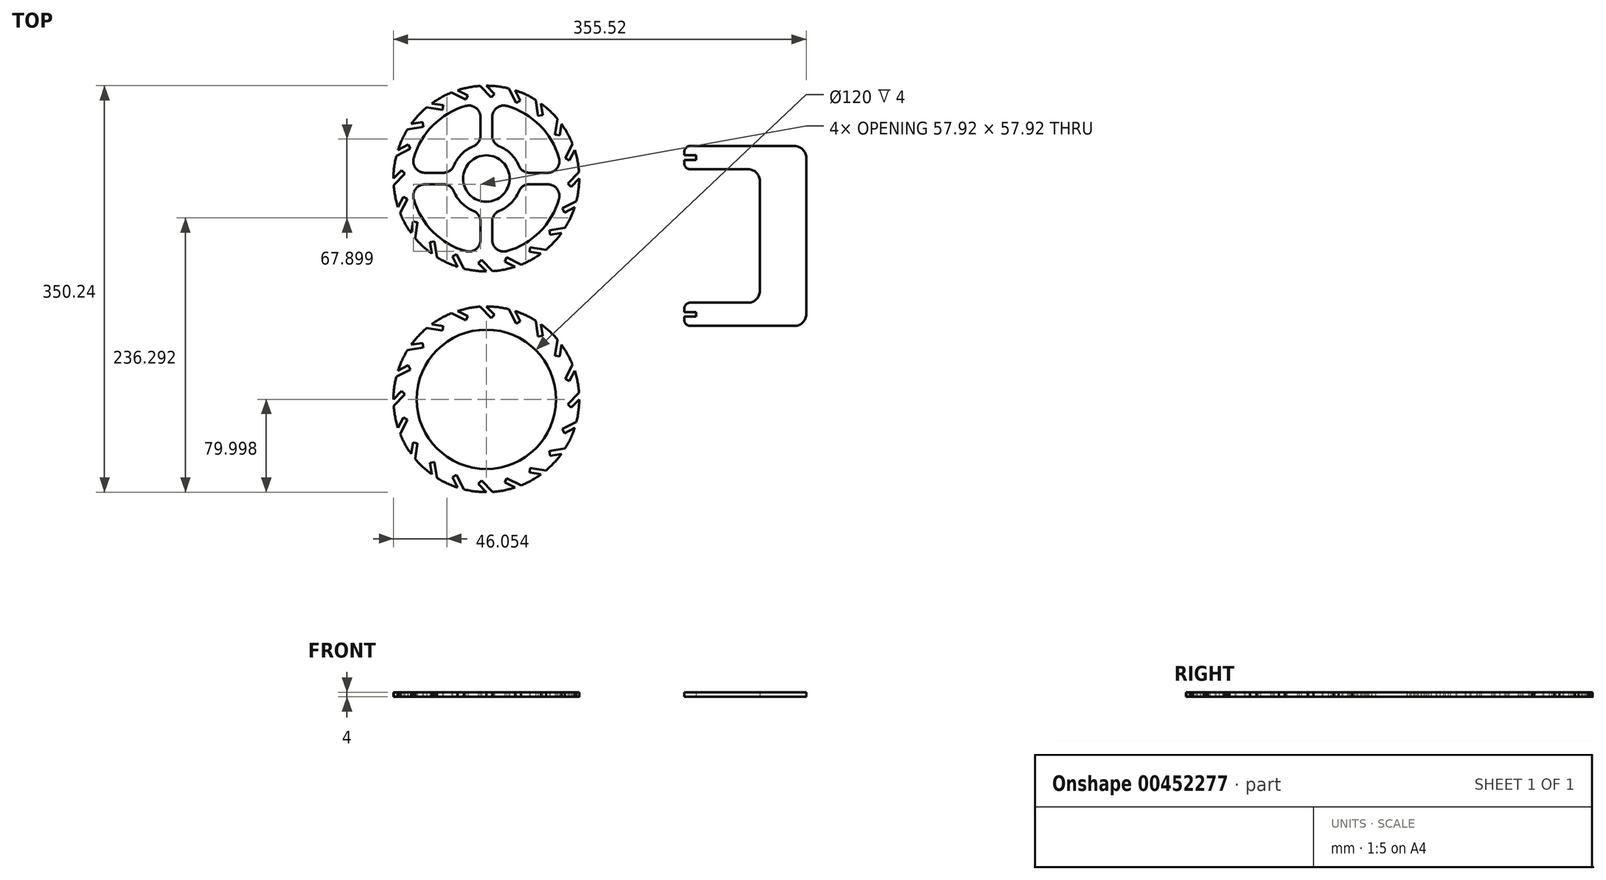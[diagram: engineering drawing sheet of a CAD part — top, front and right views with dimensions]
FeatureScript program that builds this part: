
annotation { "Feature Type Name" : "Feature", "Feature Type Description" : "" }
export const myFeature = defineFeature(function(context is Context, id is Id, definition is map)
    precondition{}
    {
        {
            var Q0;
            Q0=qCreatedBy(makeId("Top.planeOp"),FACE);
            var sketch = newSketch(context, id + "F0", { "sketchPlane" : qUnion([Q0])});
            skLineSegment(sketch, "E0", {"start": v(-117.76, 175.12) * mm, "end": v(-110.69, 168.05) * mm});
            skLineSegment(sketch, "E1", {"start": v(-110.69, 168.05) * mm, "end": v(-113.51, 165.22) * mm});
            skLineSegment(sketch, "E2", {"start": v(-133.57, 166.67) * mm, "end": v(-135.38, 163.1) * mm});
            skLineSegment(sketch, "E3", {"start": v(-142.48, 171.2) * mm, "end": v(-133.57, 166.67) * mm});
            skLineSegment(sketch, "E4", {"start": v(-135.38, 163.1) * mm, "end": v(-147.62, 169.34) * mm});
            skLineSegment(sketch, "E5", {"start": v(-154.9, 158.28) * mm, "end": v(-155.53, 154.33) * mm});
            skLineSegment(sketch, "E6", {"start": v(-164.78, 159.84) * mm, "end": v(-154.9, 158.28) * mm});
            skLineSegment(sketch, "E7", {"start": v(-155.53, 154.33) * mm, "end": v(-169.1, 156.48) * mm});
            skLineSegment(sketch, "E8", {"start": v(-172.6, 143.7) * mm, "end": v(-171.98, 139.76) * mm});
            skLineSegment(sketch, "E9", {"start": v(-182.48, 142.14) * mm, "end": v(-172.6, 143.7) * mm});
            skLineSegment(sketch, "E10", {"start": v(-171.98, 139.76) * mm, "end": v(-185.54, 137.6) * mm});
            skLineSegment(sketch, "E11", {"start": v(-184.93, 124.38) * mm, "end": v(-183.11, 120.82) * mm});
            skLineSegment(sketch, "E12", {"start": v(-193.84, 119.84) * mm, "end": v(-184.93, 124.38) * mm});
            skLineSegment(sketch, "E13", {"start": v(-183.11, 120.82) * mm, "end": v(-195.35, 114.58) * mm});
            skLineSegment(sketch, "E14", {"start": v(-190.69, 102.2) * mm, "end": v(-187.86, 99.36) * mm});
            skLineSegment(sketch, "E15", {"start": v(-197.76, 95.12) * mm, "end": v(-190.69, 102.2) * mm});
            skLineSegment(sketch, "E16", {"start": v(-187.86, 99.36) * mm, "end": v(-197.57, 89.65) * mm});
            skLineSegment(sketch, "E17", {"start": v(-189.3, 79.31) * mm, "end": v(-185.74, 77.5) * mm});
            skLineSegment(sketch, "E18", {"start": v(-193.84, 70.4) * mm, "end": v(-189.3, 79.31) * mm});
            skLineSegment(sketch, "E19", {"start": v(-185.74, 77.5) * mm, "end": v(-191.97, 65.26) * mm});
            skLineSegment(sketch, "E20", {"start": v(-180.91, 57.98) * mm, "end": v(-176.96, 57.35) * mm});
            skLineSegment(sketch, "E21", {"start": v(-182.48, 48.1) * mm, "end": v(-180.91, 57.98) * mm});
            skLineSegment(sketch, "E22", {"start": v(-176.96, 57.35) * mm, "end": v(-179.11, 43.78) * mm});
            skLineSegment(sketch, "E23", {"start": v(-166.34, 40.28) * mm, "end": v(-162.4, 40.9) * mm});
            skLineSegment(sketch, "E24", {"start": v(-164.78, 30.4) * mm, "end": v(-166.34, 40.28) * mm});
            skLineSegment(sketch, "E25", {"start": v(-162.4, 40.9) * mm, "end": v(-160.24, 27.34) * mm});
            skLineSegment(sketch, "E26", {"start": v(-147.02, 27.95) * mm, "end": v(-143.45, 29.76) * mm});
            skLineSegment(sketch, "E27", {"start": v(-142.48, 19.04) * mm, "end": v(-147.02, 27.95) * mm});
            skLineSegment(sketch, "E28", {"start": v(-143.45, 29.76) * mm, "end": v(-137.22, 17.52) * mm});
            skLineSegment(sketch, "E29", {"start": v(-124.83, 22.2) * mm, "end": v(-122, 25.02) * mm});
            skLineSegment(sketch, "E30", {"start": v(-117.76, 15.12) * mm, "end": v(-124.83, 22.2) * mm});
            skLineSegment(sketch, "E31", {"start": v(-122, 25.02) * mm, "end": v(-112.29, 15.3) * mm});
            skLineSegment(sketch, "E32", {"start": v(-101.95, 23.58) * mm, "end": v(-100.13, 27.14) * mm});
            skLineSegment(sketch, "E33", {"start": v(-93.04, 19.04) * mm, "end": v(-101.95, 23.58) * mm});
            skLineSegment(sketch, "E34", {"start": v(-100.13, 27.14) * mm, "end": v(-87.9, 20.9) * mm});
            skLineSegment(sketch, "E35", {"start": v(-80.61, 31.96) * mm, "end": v(-79.98, 35.92) * mm});
            skLineSegment(sketch, "E36", {"start": v(-70.73, 30.4) * mm, "end": v(-80.61, 31.96) * mm});
            skLineSegment(sketch, "E37", {"start": v(-79.98, 35.92) * mm, "end": v(-66.42, 33.77) * mm});
            skLineSegment(sketch, "E38", {"start": v(-62.91, 46.53) * mm, "end": v(-63.54, 50.49) * mm});
            skLineSegment(sketch, "E39", {"start": v(-53.04, 48.1) * mm, "end": v(-62.91, 46.53) * mm});
            skLineSegment(sketch, "E40", {"start": v(-63.54, 50.49) * mm, "end": v(-49.97, 52.63) * mm});
            skLineSegment(sketch, "E41", {"start": v(-50.58, 65.86) * mm, "end": v(-52.4, 69.42) * mm});
            skLineSegment(sketch, "E42", {"start": v(-41.67, 70.4) * mm, "end": v(-50.58, 65.86) * mm});
            skLineSegment(sketch, "E43", {"start": v(-52.4, 69.42) * mm, "end": v(-40.16, 75.66) * mm});
            skLineSegment(sketch, "E44", {"start": v(-44.83, 88.05) * mm, "end": v(-47.66, 90.88) * mm});
            skLineSegment(sketch, "E45", {"start": v(-37.76, 95.12) * mm, "end": v(-44.83, 88.05) * mm});
            skLineSegment(sketch, "E46", {"start": v(-47.66, 90.88) * mm, "end": v(-37.94, 100.6) * mm});
            skLineSegment(sketch, "E47", {"start": v(-46.21, 110.93) * mm, "end": v(-49.78, 112.75) * mm});
            skLineSegment(sketch, "E48", {"start": v(-41.67, 119.84) * mm, "end": v(-46.21, 110.93) * mm});
            skLineSegment(sketch, "E49", {"start": v(-49.78, 112.75) * mm, "end": v(-43.54, 124.99) * mm});
            skLineSegment(sketch, "E50", {"start": v(-54.6, 132.27) * mm, "end": v(-58.55, 132.9) * mm});
            skLineSegment(sketch, "E51", {"start": v(-53.04, 142.14) * mm, "end": v(-54.6, 132.27) * mm});
            skLineSegment(sketch, "E52", {"start": v(-58.55, 132.9) * mm, "end": v(-56.4, 146.46) * mm});
            skLineSegment(sketch, "E53", {"start": v(-69.17, 149.97) * mm, "end": v(-73.12, 149.34) * mm});
            skLineSegment(sketch, "E54", {"start": v(-70.73, 159.84) * mm, "end": v(-69.17, 149.97) * mm});
            skLineSegment(sketch, "E55", {"start": v(-73.12, 149.34) * mm, "end": v(-75.27, 162.9) * mm});
            skLineSegment(sketch, "E56", {"start": v(-88.5, 162.3) * mm, "end": v(-92.06, 160.48) * mm});
            skLineSegment(sketch, "E57", {"start": v(-93.04, 171.2) * mm, "end": v(-88.5, 162.3) * mm});
            skLineSegment(sketch, "E58", {"start": v(-92.06, 160.48) * mm, "end": v(-98.3, 172.72) * mm});
            skArc(sketch, "E59", {"start": v(-123.23, 174.93) * mm, "mid": v(-132.97, 173.66) * mm, "end": v(-142.48, 171.2) * mm});
            skArc(sketch, "E60", {"start": v(-169.1, 156.48) * mm, "mid": v(-176.23, 149.72) * mm, "end": v(-182.48, 142.14) * mm});
            skArc(sketch, "E61", {"start": v(-185.54, 137.6) * mm, "mid": v(-190.24, 128.98) * mm, "end": v(-193.84, 119.84) * mm});
            skArc(sketch, "E62", {"start": v(-195.35, 114.58) * mm, "mid": v(-197.15, 104.93) * mm, "end": v(-197.76, 95.12) * mm});
            skArc(sketch, "E63", {"start": v(-197.57, 89.65) * mm, "mid": v(-196.3, 79.91) * mm, "end": v(-193.84, 70.4) * mm});
            skArc(sketch, "E64", {"start": v(-191.97, 65.26) * mm, "mid": v(-187.75, 56.39) * mm, "end": v(-182.48, 48.1) * mm});
            skArc(sketch, "E65", {"start": v(-179.11, 43.78) * mm, "mid": v(-172.36, 36.65) * mm, "end": v(-164.78, 30.4) * mm});
            skArc(sketch, "E66", {"start": v(-160.24, 27.34) * mm, "mid": v(-151.62, 22.64) * mm, "end": v(-142.48, 19.04) * mm});
            skArc(sketch, "E67", {"start": v(-137.22, 17.52) * mm, "mid": v(-127.56, 15.72) * mm, "end": v(-117.76, 15.12) * mm});
            skArc(sketch, "E68", {"start": v(-112.29, 15.3) * mm, "mid": v(-102.55, 16.58) * mm, "end": v(-93.04, 19.04) * mm});
            skArc(sketch, "E69", {"start": v(-87.9, 20.9) * mm, "mid": v(-79.02, 25.13) * mm, "end": v(-70.73, 30.4) * mm});
            skArc(sketch, "E70", {"start": v(-66.42, 33.77) * mm, "mid": v(-59.29, 40.52) * mm, "end": v(-53.04, 48.1) * mm});
            skArc(sketch, "E71", {"start": v(-49.97, 52.63) * mm, "mid": v(-45.28, 61.26) * mm, "end": v(-41.67, 70.4) * mm});
            skArc(sketch, "E72", {"start": v(-40.16, 75.66) * mm, "mid": v(-38.36, 85.32) * mm, "end": v(-37.76, 95.12) * mm});
            skArc(sketch, "E73", {"start": v(-37.94, 100.6) * mm, "mid": v(-39.22, 110.33) * mm, "end": v(-41.67, 119.84) * mm});
            skArc(sketch, "E74", {"start": v(-43.54, 124.99) * mm, "mid": v(-47.76, 133.86) * mm, "end": v(-53.04, 142.14) * mm});
            skArc(sketch, "E75", {"start": v(-56.4, 146.46) * mm, "mid": v(-63.16, 153.6) * mm, "end": v(-70.73, 159.84) * mm});
            skArc(sketch, "E76", {"start": v(-98.3, 172.72) * mm, "mid": v(-107.95, 174.52) * mm, "end": v(-117.76, 175.12) * mm});
            skArc(sketch, "E77", {"start": v(-75.27, 162.9) * mm, "mid": v(-83.9, 167.6) * mm, "end": v(-93.04, 171.2) * mm});
            skLineSegment(sketch, "E78", {"start": v(-154.84, 90.13) * mm, "end": v(-170.67, 90.13) * mm});
            skLineSegment(sketch, "E79", {"start": v(-154.84, 100.11) * mm, "end": v(-170.67, 100.11) * mm});
            skLineSegment(sketch, "E80", {"start": v(-122.75, 58.04) * mm, "end": v(-122.75, 42.2) * mm});
            skLineSegment(sketch, "E81", {"start": v(-112.76, 58.04) * mm, "end": v(-112.76, 42.2) * mm});
            skLineSegment(sketch, "E82", {"start": v(-80.67, 90.13) * mm, "end": v(-64.84, 90.13) * mm});
            skLineSegment(sketch, "E83", {"start": v(-80.67, 100.11) * mm, "end": v(-64.84, 100.11) * mm});
            skLineSegment(sketch, "E84", {"start": v(-112.76, 132.2) * mm, "end": v(-112.76, 148.04) * mm});
            skLineSegment(sketch, "E85", {"start": v(-122.75, 132.2) * mm, "end": v(-122.75, 148.04) * mm});
            skArc(sketch, "E86", {"start": v(-145.57, 83.88) * mm, "mid": v(-138.97, 73.9) * mm, "end": v(-129, 67.3) * mm});
            skArc(sketch, "E87", {"start": v(-180.3, 77.4) * mm, "mid": v(-163.72, 49.16) * mm, "end": v(-135.47, 32.58) * mm});
            skArc(sketch, "E88", {"start": v(-106.51, 67.3) * mm, "mid": v(-96.54, 73.9) * mm, "end": v(-89.94, 83.88) * mm});
            skArc(sketch, "E89", {"start": v(-100.04, 32.58) * mm, "mid": v(-71.8, 49.16) * mm, "end": v(-55.22, 77.4) * mm});
            skArc(sketch, "E90", {"start": v(-135.47, 157.66) * mm, "mid": v(-163.72, 141.08) * mm, "end": v(-180.3, 112.84) * mm});
            skArc(sketch, "E91", {"start": v(-55.22, 112.84) * mm, "mid": v(-71.8, 141.08) * mm, "end": v(-100.04, 157.66) * mm});
            skArc(sketch, "E92", {"start": v(-129, 122.93) * mm, "mid": v(-138.97, 116.33) * mm, "end": v(-145.57, 106.37) * mm});
            skArc(sketch, "E93", {"start": v(-89.94, 106.37) * mm, "mid": v(-96.54, 116.33) * mm, "end": v(-106.51, 122.93) * mm});
            skArc(sketch, "E94", {"start": v(-180.3, 112.84) * mm, "mid": v(-178.65, 104.08) * mm, "end": v(-170.67, 100.11) * mm});
            skArc(sketch, "E95", {"start": v(-154.84, 100.11) * mm, "mid": v(-149.25, 101.82) * mm, "end": v(-145.57, 106.37) * mm});
            skArc(sketch, "E96", {"start": v(-129, 122.93) * mm, "mid": v(-124.46, 126.61) * mm, "end": v(-122.75, 132.2) * mm});
            skArc(sketch, "E97", {"start": v(-112.76, 132.2) * mm, "mid": v(-111.06, 126.61) * mm, "end": v(-106.51, 122.93) * mm});
            skArc(sketch, "E98", {"start": v(-89.94, 106.37) * mm, "mid": v(-86.26, 101.82) * mm, "end": v(-80.67, 100.11) * mm});
            skArc(sketch, "E99", {"start": v(-80.67, 90.13) * mm, "mid": v(-86.26, 88.42) * mm, "end": v(-89.94, 83.88) * mm});
            skArc(sketch, "E100", {"start": v(-106.51, 67.3) * mm, "mid": v(-111.06, 63.63) * mm, "end": v(-112.76, 58.04) * mm});
            skArc(sketch, "E101", {"start": v(-122.75, 58.04) * mm, "mid": v(-124.46, 63.63) * mm, "end": v(-129, 67.3) * mm});
            skArc(sketch, "E102", {"start": v(-145.57, 83.88) * mm, "mid": v(-149.25, 88.42) * mm, "end": v(-154.84, 90.13) * mm});
            skArc(sketch, "E103", {"start": v(-122.75, 148.04) * mm, "mid": v(-126.72, 156.02) * mm, "end": v(-135.47, 157.66) * mm});
            skArc(sketch, "E104", {"start": v(-100.04, 157.66) * mm, "mid": v(-108.8, 156.02) * mm, "end": v(-112.76, 148.04) * mm});
            skArc(sketch, "E105", {"start": v(-64.84, 100.11) * mm, "mid": v(-56.86, 104.08) * mm, "end": v(-55.22, 112.84) * mm});
            skArc(sketch, "E106", {"start": v(-55.22, 77.4) * mm, "mid": v(-56.86, 86.16) * mm, "end": v(-64.84, 90.13) * mm});
            skArc(sketch, "E107", {"start": v(-112.76, 42.2) * mm, "mid": v(-108.8, 34.23) * mm, "end": v(-100.04, 32.58) * mm});
            skArc(sketch, "E108", {"start": v(-135.47, 32.58) * mm, "mid": v(-126.72, 34.23) * mm, "end": v(-122.75, 42.2) * mm});
            skArc(sketch, "E109", {"start": v(-170.67, 90.13) * mm, "mid": v(-178.65, 86.16) * mm, "end": v(-180.3, 77.4) * mm});
            skCircle(sketch, "E110", {"center": v(-117.76, 95.12) * mm, "radius": 20 * mm});
            skLineSegment(sketch, "E111", {"start": v(-113.51, 165.22) * mm, "end": v(-123.23, 174.93) * mm});
            skLineSegment(sketch, "E112", {"start": v(-117.76, -15.12) * mm, "end": v(-110.69, -22.2) * mm});
            skLineSegment(sketch, "E113", {"start": v(-110.69, -22.2) * mm, "end": v(-113.51, -25.02) * mm});
            skLineSegment(sketch, "E114", {"start": v(-133.57, -23.58) * mm, "end": v(-135.38, -27.14) * mm});
            skLineSegment(sketch, "E115", {"start": v(-142.48, -19.04) * mm, "end": v(-133.57, -23.58) * mm});
            skLineSegment(sketch, "E116", {"start": v(-135.38, -27.14) * mm, "end": v(-147.62, -20.9) * mm});
            skLineSegment(sketch, "E117", {"start": v(-154.9, -31.96) * mm, "end": v(-155.53, -35.92) * mm});
            skLineSegment(sketch, "E118", {"start": v(-164.78, -30.4) * mm, "end": v(-154.9, -31.96) * mm});
            skLineSegment(sketch, "E119", {"start": v(-155.53, -35.92) * mm, "end": v(-169.1, -33.77) * mm});
            skLineSegment(sketch, "E120", {"start": v(-172.6, -46.53) * mm, "end": v(-171.98, -50.49) * mm});
            skLineSegment(sketch, "E121", {"start": v(-182.48, -48.1) * mm, "end": v(-172.6, -46.53) * mm});
            skLineSegment(sketch, "E122", {"start": v(-171.98, -50.49) * mm, "end": v(-185.54, -52.63) * mm});
            skLineSegment(sketch, "E123", {"start": v(-184.93, -65.86) * mm, "end": v(-183.11, -69.42) * mm});
            skLineSegment(sketch, "E124", {"start": v(-193.84, -70.4) * mm, "end": v(-184.93, -65.86) * mm});
            skLineSegment(sketch, "E125", {"start": v(-183.11, -69.42) * mm, "end": v(-195.35, -75.66) * mm});
            skLineSegment(sketch, "E126", {"start": v(-190.69, -88.05) * mm, "end": v(-187.86, -90.88) * mm});
            skLineSegment(sketch, "E127", {"start": v(-197.76, -95.12) * mm, "end": v(-190.69, -88.05) * mm});
            skLineSegment(sketch, "E128", {"start": v(-187.86, -90.88) * mm, "end": v(-197.57, -100.6) * mm});
            skLineSegment(sketch, "E129", {"start": v(-189.3, -110.93) * mm, "end": v(-185.74, -112.75) * mm});
            skLineSegment(sketch, "E130", {"start": v(-193.84, -119.84) * mm, "end": v(-189.3, -110.93) * mm});
            skLineSegment(sketch, "E131", {"start": v(-185.74, -112.75) * mm, "end": v(-191.97, -124.99) * mm});
            skLineSegment(sketch, "E132", {"start": v(-180.91, -132.27) * mm, "end": v(-176.96, -132.9) * mm});
            skLineSegment(sketch, "E133", {"start": v(-182.48, -142.14) * mm, "end": v(-180.91, -132.27) * mm});
            skLineSegment(sketch, "E134", {"start": v(-176.96, -132.9) * mm, "end": v(-179.11, -146.46) * mm});
            skLineSegment(sketch, "E135", {"start": v(-166.34, -149.97) * mm, "end": v(-162.4, -149.34) * mm});
            skLineSegment(sketch, "E136", {"start": v(-164.78, -159.84) * mm, "end": v(-166.34, -149.97) * mm});
            skLineSegment(sketch, "E137", {"start": v(-162.4, -149.34) * mm, "end": v(-160.24, -162.9) * mm});
            skLineSegment(sketch, "E138", {"start": v(-147.02, -162.3) * mm, "end": v(-143.45, -160.48) * mm});
            skLineSegment(sketch, "E139", {"start": v(-142.48, -171.2) * mm, "end": v(-147.02, -162.3) * mm});
            skLineSegment(sketch, "E140", {"start": v(-143.45, -160.48) * mm, "end": v(-137.22, -172.72) * mm});
            skLineSegment(sketch, "E141", {"start": v(-124.83, -168.05) * mm, "end": v(-122, -165.22) * mm});
            skLineSegment(sketch, "E142", {"start": v(-117.76, -175.12) * mm, "end": v(-124.83, -168.05) * mm});
            skLineSegment(sketch, "E143", {"start": v(-122, -165.22) * mm, "end": v(-112.29, -174.93) * mm});
            skLineSegment(sketch, "E144", {"start": v(-101.95, -166.67) * mm, "end": v(-100.13, -163.1) * mm});
            skLineSegment(sketch, "E145", {"start": v(-93.04, -171.2) * mm, "end": v(-101.95, -166.67) * mm});
            skLineSegment(sketch, "E146", {"start": v(-100.13, -163.1) * mm, "end": v(-87.9, -169.34) * mm});
            skLineSegment(sketch, "E147", {"start": v(-80.61, -158.28) * mm, "end": v(-79.98, -154.33) * mm});
            skLineSegment(sketch, "E148", {"start": v(-70.73, -159.84) * mm, "end": v(-80.61, -158.28) * mm});
            skLineSegment(sketch, "E149", {"start": v(-79.98, -154.33) * mm, "end": v(-66.42, -156.48) * mm});
            skLineSegment(sketch, "E150", {"start": v(-62.91, -143.7) * mm, "end": v(-63.54, -139.76) * mm});
            skLineSegment(sketch, "E151", {"start": v(-53.04, -142.14) * mm, "end": v(-62.91, -143.7) * mm});
            skLineSegment(sketch, "E152", {"start": v(-63.54, -139.76) * mm, "end": v(-49.97, -137.6) * mm});
            skLineSegment(sketch, "E153", {"start": v(-50.58, -124.38) * mm, "end": v(-52.4, -120.82) * mm});
            skLineSegment(sketch, "E154", {"start": v(-41.67, -119.84) * mm, "end": v(-50.58, -124.38) * mm});
            skLineSegment(sketch, "E155", {"start": v(-52.4, -120.82) * mm, "end": v(-40.16, -114.58) * mm});
            skLineSegment(sketch, "E156", {"start": v(-44.83, -102.2) * mm, "end": v(-47.66, -99.36) * mm});
            skLineSegment(sketch, "E157", {"start": v(-37.76, -95.12) * mm, "end": v(-44.83, -102.2) * mm});
            skLineSegment(sketch, "E158", {"start": v(-47.66, -99.36) * mm, "end": v(-37.94, -89.65) * mm});
            skLineSegment(sketch, "E159", {"start": v(-46.21, -79.31) * mm, "end": v(-49.78, -77.5) * mm});
            skLineSegment(sketch, "E160", {"start": v(-41.67, -70.4) * mm, "end": v(-46.21, -79.31) * mm});
            skLineSegment(sketch, "E161", {"start": v(-49.78, -77.5) * mm, "end": v(-43.54, -65.26) * mm});
            skLineSegment(sketch, "E162", {"start": v(-54.6, -57.98) * mm, "end": v(-58.55, -57.35) * mm});
            skLineSegment(sketch, "E163", {"start": v(-53.04, -48.1) * mm, "end": v(-54.6, -57.98) * mm});
            skLineSegment(sketch, "E164", {"start": v(-58.55, -57.35) * mm, "end": v(-56.4, -43.78) * mm});
            skLineSegment(sketch, "E165", {"start": v(-69.17, -40.28) * mm, "end": v(-73.12, -40.9) * mm});
            skLineSegment(sketch, "E166", {"start": v(-70.73, -30.4) * mm, "end": v(-69.17, -40.28) * mm});
            skLineSegment(sketch, "E167", {"start": v(-73.12, -40.9) * mm, "end": v(-75.27, -27.34) * mm});
            skLineSegment(sketch, "E168", {"start": v(-88.5, -27.95) * mm, "end": v(-92.06, -29.76) * mm});
            skLineSegment(sketch, "E169", {"start": v(-93.04, -19.04) * mm, "end": v(-88.5, -27.95) * mm});
            skLineSegment(sketch, "E170", {"start": v(-92.06, -29.76) * mm, "end": v(-98.3, -17.52) * mm});
            skArc(sketch, "E171", {"start": v(-123.23, -15.3) * mm, "mid": v(-132.97, -16.58) * mm, "end": v(-142.48, -19.04) * mm});
            skArc(sketch, "E172", {"start": v(-169.1, -33.77) * mm, "mid": v(-176.23, -40.52) * mm, "end": v(-182.48, -48.1) * mm});
            skArc(sketch, "E173", {"start": v(-185.54, -52.63) * mm, "mid": v(-190.24, -61.26) * mm, "end": v(-193.84, -70.4) * mm});
            skArc(sketch, "E174", {"start": v(-195.35, -75.66) * mm, "mid": v(-197.15, -85.32) * mm, "end": v(-197.76, -95.12) * mm});
            skArc(sketch, "E175", {"start": v(-197.57, -100.6) * mm, "mid": v(-196.3, -110.33) * mm, "end": v(-193.84, -119.84) * mm});
            skArc(sketch, "E176", {"start": v(-191.97, -124.99) * mm, "mid": v(-187.75, -133.86) * mm, "end": v(-182.48, -142.14) * mm});
            skArc(sketch, "E177", {"start": v(-179.11, -146.46) * mm, "mid": v(-172.36, -153.6) * mm, "end": v(-164.78, -159.84) * mm});
            skArc(sketch, "E178", {"start": v(-160.24, -162.9) * mm, "mid": v(-151.62, -167.6) * mm, "end": v(-142.48, -171.2) * mm});
            skArc(sketch, "E179", {"start": v(-137.22, -172.72) * mm, "mid": v(-127.56, -174.52) * mm, "end": v(-117.76, -175.12) * mm});
            skArc(sketch, "E180", {"start": v(-112.29, -174.93) * mm, "mid": v(-102.55, -173.66) * mm, "end": v(-93.04, -171.2) * mm});
            skArc(sketch, "E181", {"start": v(-87.9, -169.34) * mm, "mid": v(-79.02, -165.12) * mm, "end": v(-70.73, -159.84) * mm});
            skArc(sketch, "E182", {"start": v(-66.42, -156.48) * mm, "mid": v(-59.29, -149.72) * mm, "end": v(-53.04, -142.14) * mm});
            skArc(sketch, "E183", {"start": v(-49.97, -137.6) * mm, "mid": v(-45.28, -128.98) * mm, "end": v(-41.67, -119.84) * mm});
            skArc(sketch, "E184", {"start": v(-40.16, -114.58) * mm, "mid": v(-38.36, -104.93) * mm, "end": v(-37.76, -95.12) * mm});
            skArc(sketch, "E185", {"start": v(-37.94, -89.65) * mm, "mid": v(-39.22, -79.91) * mm, "end": v(-41.67, -70.4) * mm});
            skArc(sketch, "E186", {"start": v(-43.54, -65.26) * mm, "mid": v(-47.76, -56.39) * mm, "end": v(-53.04, -48.1) * mm});
            skArc(sketch, "E187", {"start": v(-56.4, -43.78) * mm, "mid": v(-63.16, -36.65) * mm, "end": v(-70.73, -30.4) * mm});
            skArc(sketch, "E188", {"start": v(-98.3, -17.52) * mm, "mid": v(-107.95, -15.72) * mm, "end": v(-117.76, -15.12) * mm});
            skArc(sketch, "E189", {"start": v(-75.27, -27.34) * mm, "mid": v(-83.9, -22.64) * mm, "end": v(-93.04, -19.04) * mm});
            skLineSegment(sketch, "E190", {"start": v(-113.51, -25.02) * mm, "end": v(-123.23, -15.3) * mm});
            skCircle(sketch, "E191", {"center": v(-117.76, -95.12) * mm, "radius": 60 * mm});
            skLineSegment(sketch, "E192", {"start": v(57.76, 123.12) * mm, "end": v(147.76, 123.12) * mm});
            skLineSegment(sketch, "E193", {"start": v(157.76, 113.12) * mm, "end": v(157.76, -21.88) * mm});
            skLineSegment(sketch, "E194", {"start": v(52.76, 118.12) * mm, "end": v(52.76, 115.12) * mm});
            skLineSegment(sketch, "E195", {"start": v(57.76, 103.12) * mm, "end": v(107.76, 103.12) * mm});
            skLineSegment(sketch, "E196", {"start": v(52.76, 111.12) * mm, "end": v(62.76, 111.12) * mm});
            skLineSegment(sketch, "E197", {"start": v(62.76, 111.12) * mm, "end": v(62.76, 115.12) * mm});
            skLineSegment(sketch, "E198", {"start": v(62.76, 115.12) * mm, "end": v(52.76, 115.12) * mm});
            skLineSegment(sketch, "E199", {"start": v(52.76, 111.12) * mm, "end": v(52.76, 108.12) * mm});
            skLineSegment(sketch, "E200", {"start": v(117.76, 93.12) * mm, "end": v(117.76, -1.88) * mm});
            skArc(sketch, "E201", {"start": v(117.76, 93.12) * mm, "mid": v(114.83, 100.2) * mm, "end": v(107.76, 103.12) * mm});
            skLineSegment(sketch, "E202", {"start": v(57.76, -31.88) * mm, "end": v(147.76, -31.88) * mm});
            skLineSegment(sketch, "E203", {"start": v(52.76, -26.88) * mm, "end": v(52.76, -23.88) * mm});
            skLineSegment(sketch, "E204", {"start": v(57.76, -11.88) * mm, "end": v(107.76, -11.88) * mm});
            skLineSegment(sketch, "E205", {"start": v(52.76, -19.88) * mm, "end": v(62.76, -19.88) * mm});
            skLineSegment(sketch, "E206", {"start": v(62.76, -19.88) * mm, "end": v(62.76, -23.88) * mm});
            skLineSegment(sketch, "E207", {"start": v(62.76, -23.88) * mm, "end": v(52.76, -23.88) * mm});
            skLineSegment(sketch, "E208", {"start": v(52.76, -19.88) * mm, "end": v(52.76, -16.88) * mm});
            skArc(sketch, "E209", {"start": v(107.76, -11.88) * mm, "mid": v(114.83, -8.95) * mm, "end": v(117.76, -1.88) * mm});
            skArc(sketch, "E210", {"start": v(57.76, -11.88) * mm, "mid": v(54.22, -13.34) * mm, "end": v(52.76, -16.88) * mm});
            skArc(sketch, "E211", {"start": v(52.76, -26.88) * mm, "mid": v(54.22, -30.41) * mm, "end": v(57.76, -31.88) * mm});
            skArc(sketch, "E212", {"start": v(57.76, 123.12) * mm, "mid": v(54.22, 121.66) * mm, "end": v(52.76, 118.12) * mm});
            skArc(sketch, "E213", {"start": v(52.76, 108.12) * mm, "mid": v(54.22, 104.59) * mm, "end": v(57.76, 103.12) * mm});
            skArc(sketch, "E214", {"start": v(-147.62, 169.34) * mm, "mid": v(-156.5, 165.12) * mm, "end": v(-164.78, 159.84) * mm});
            skArc(sketch, "E215", {"start": v(-147.62, -20.9) * mm, "mid": v(-156.5, -25.13) * mm, "end": v(-164.78, -30.4) * mm});
            skPoint(sketch, "E216.newPointB", {"position": v(157.76, 113.12) * mm});
            skArc(sketch, "E216.filletArc", {"start": v(157.76, 113.12) * mm, "mid": v(154.83, 120.2) * mm, "end": v(147.76, 123.12) * mm});
            skPoint(sketch, "E217.newPointB", {"position": v(157.76, -21.88) * mm});
            skArc(sketch, "E217.filletArc", {"start": v(147.76, -31.88) * mm, "mid": v(154.83, -28.95) * mm, "end": v(157.76, -21.88) * mm});
            skSolve(sketch);
        }
        {
            var Q0;
            Q0=qSketchRegion(id+"F0",true);
            extrude(context, id + "F1", {"entities" : qUnion([Q0]), "depth" : 4 * mm});
        }
    });
